# Revit family: CAME_Турникет_Калитка_SALOON40_Автоматическая
name_source: partatom
category: Специальное оборудование
units: mm (PartAtom-declared; Revit-internal decimal feet)

## family parameters
Всегда вертикально = Да
На основе рабочей плоскости = Нет
Общий = Нет
При загрузке вырезать с полостями = Нет
Размер круглого соединителя = Использовать диаметр
Тип детали = Нормальный
Точка расчета площади = Нет

## types (2) — shared parameters
ADSK_URL документации изделия = https://camerussia.com
ADSK_URL страницы изделия = https://camerussia.com
ADSK_Версия Revit = 2019
ADSK_Версия семейства = 1.0
ADSK_Группирование = SALOON
ADSK_Единица измерения = шт.
ADSK_Завод-изготовитель = CAME
ADSK_Классификация нагрузок = Прочее
ADSK_Код изделия = Код КСР 26.30.50.119.61.2.07.09
ADSK_Количество = 1
ADSK_Количество фаз = 1
ADSK_Коэффициент мощности = 0.96
ADSK_Марка = АРТ:001PSSLN40
ADSK_Масса = 20
ADSK_Масса_Текст = 20
ADSK_Наименование = Турникет-калитка моторизованная SALOON 40
ADSK_Наименование краткое = Турникет-калитка SALOON 40
ADSK_Напряжение = 230 В
ADSK_Номинальная мощность = 120 Вт
ADSK_Обозначение = ТУ 26.30.50-001-89603926-2021
ADSK_Полная мощность = 125 В·А
ADSK_Размер_Высота = 1008 мм
ADSK_Размер_Диаметр = 120 мм
BL_BIM library = https://bimlib.pro
CAME_Время открывания (с) = 1
CAME_Диапазон рабочих температур (°C) = -20 ÷ +55
CAME_Интенсивность использования (%) = ИНТЕНСИВНОЕ
CAME_Класс защиты (IP) = 40
CAME_Максимальное количество проходов в минуту = 12
CAME_Напряжение электропитания двигателя (В) = 24 В
CAME_Тип механизма турникета = моторизованный
URL = https://camerussia.com
Группа модели = Турникеты
Изготовитель = CAME
Нержавеющая сталь = Крепление : Нержавеющая сталь
Описание = Турникет-калитка моторизованная (без створки). Оснащена платой управления и светодиодным индикатором. Корпус - алюминий. Сервопозиционный электропривод створки с определением препятствий и автоматической разблокировкой при отключении электроэнергии. Встроенный блок питания.
Хром = Крепление : Хром
в1 = CAME_КомплектКрепления_ГоризонтальныхПланок_SALOON40_ДляОграждений : Хром
в2 = CAME_КомплектКрепления_ГоризонтальныхПланок_SALOON40_ДляОграждений : Нержавеющая сталь

## per-type parameters (varying)
| type | ADSK_Размер_Ширина | Створка | Ширина створки |
| 900 | 1020 мм | CAME_Створка_SALOON40 : 900 мм | 900 мм |
| 1200 | 1320 мм | CAME_Створка_SALOON40 : 1200 мм | 1200 мм |
